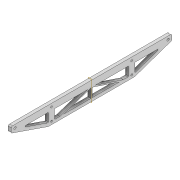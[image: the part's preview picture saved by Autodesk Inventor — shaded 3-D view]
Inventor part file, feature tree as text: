
AUTODESK INVENTOR PART (.ipt)
format: ipt  version: 2022 (Build 260153000, 153)  size: 191,488 bytes
history: native  units: mm
features: extrude x3, sketch x3, fillet x2, mirror x1
ambient origin geometry x8: Origin, YZ Plane, XZ Plane, XY Plane, X Axis, Y Axis, Z Axis, Center Point
bodies: Solid1 (feature_tree)
feature tree (9):
  extrude  "Extrusion1"  Depth=10.0mm
  fillet  "Fillet1"  Radius=3.9mm
  extrude  "Extrusion2"  Depth=3.9mm
  mirror  "Mirror1"
  extrude  "Extrusion3"  Depth=5.0mm TaperAngle=0.0deg
  fillet  "Fillet3"  Radius=2.0mm
  sketch  "Sketch1"  dims[d0=260.0mm d1=10.0mm d2=3.9mm]
  sketch  "Sketch2"  dims[d3=6.0mm d4=3.9mm]
  sketch  "Sketch4"  dims[d5=6.0mm d6=5.0mm d7=0.0mm d8=2.0mm d15=3.0mm d16=20.0mm d17=5.0mm d18=10.0mm d20=59.0mm d21=5.0mm d22=0.0mm d23=5.0mm d25=3.0mm d27=59.0mm d28=3.0mm d29=59.0mm d32=5.0mm d33=5.0mm d34=5.0mm d35=0.0mm d36=1.0mm d37=2.0mm d38=2.0mm d39=1.0mm d40=1.0mm]
